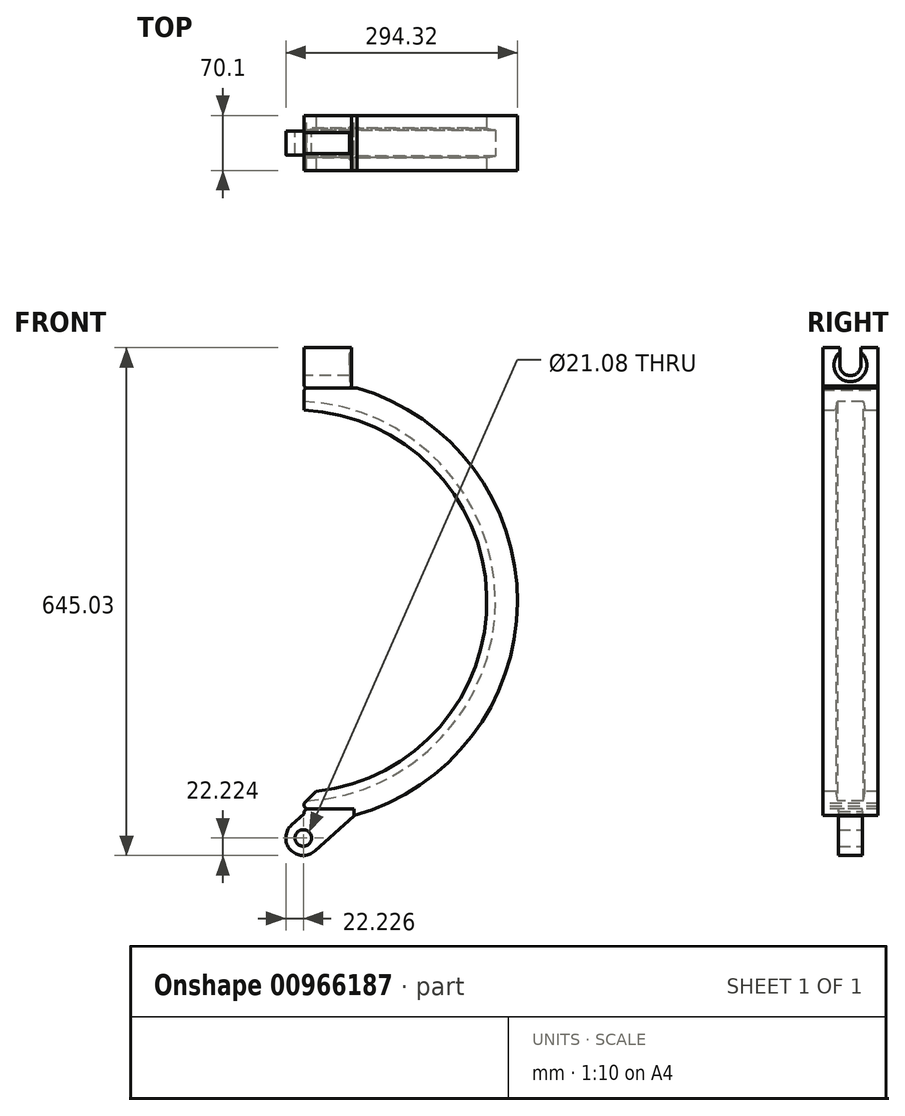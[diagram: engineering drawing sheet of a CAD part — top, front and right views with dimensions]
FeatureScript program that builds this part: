
annotation { "Feature Type Name" : "Feature", "Feature Type Description" : "" }
export const myFeature = defineFeature(function(context is Context, id is Id, definition is map)
    precondition{}
    {
        {
            var Q0;
            Q0=qCreatedBy(makeId("Front.planeOp"),FACE);
            var sketch = newSketch(context, id + "F0", { "sketchPlane" : qUnion([Q0])});
            skArc(sketch, "E0", {"start": v(11.02, -281.79) * mm, "mid": v(282, 0) * mm, "end": v(11.02, 281.79) * mm});
            skArc(sketch, "E1", {"start": v(11.02, -242.75) * mm, "mid": v(243, 0) * mm, "end": v(11.02, 242.75) * mm});
            skLineSegment(sketch, "E2", {"start": v(11.02, 281.79) * mm, "end": v(11.02, 242.75) * mm});
            skLineSegment(sketch, "E3.trimOffspring", {"start": v(11.02, -242.75) * mm, "end": v(11.02, -281.79) * mm});
            skSolve(sketch);
        }
        {
            var Q0;
            Q0=makeQuery(id+"F0.imprint","IMPRINT",FACE,{"disambiguationData":[TD([[makeQuery(id+"F0.imprint","IMPRINT",EDGE,{"derivedFrom":sQuery(id+"F0.wireOp",EDGE,"E0")}),1.0]])]});
            extrude(context, id + "F1", {"entities" : qUnion([Q0]), "depth" : 70.1 * mm, "offsetDistance" : 25.4 * mm});
        }
        {
            var Q0;
            Q0=makeQuery(id+"F1.opExtrude","SWEPT_FACE",FACE,{"disambiguationData":[OSD([sQuery(id+"F0.wireOp",EDGE,"E2")])]});
            var sketch = newSketch(context, id + "F2", { "sketchPlane" : qUnion([Q0])});
            skLineSegment(sketch, "E4", {"start": v(16.4, 242.75) * mm, "end": v(18.52, 253.68) * mm});
            skLineSegment(sketch, "E5", {"start": v(18.52, 253.68) * mm, "end": v(51.58, 253.68) * mm});
            skLineSegment(sketch, "E6", {"start": v(51.58, 253.68) * mm, "end": v(53.7, 242.75) * mm});
            skSolve(sketch);
        }
        {
            var Q0;
            {var subQ0=sQuery(id+"F2.wireOp",EDGE,"E4");Q0=makeQuery(id+"F2.imprint","IMPRINT",FACE,{"disambiguationData":[TD([[makeQuery(id+"F2.imprint","IMPRINT",EDGE,{"derivedFrom":subQ0}),-1.0]])]});}
            var Q1;
            Q1=makeQuery(id+"F1.opExtrude","CAP_EDGE",EDGE,{"disambiguationData":[OSD([sQuery(id+"F0.wireOp",EDGE,"E1")])],"isStart":false});
            revolve(context, id + "F3", {"operationType" : NewBodyOperationType.REMOVE, "surfaceOperationType" : NewSurfaceOperationType.NEW, "entities" : qUnion([Q0]), "axis" : qUnion([Q1]), "revolveType" : RevolveType.FULL, "oppositeDirection" : true});
        }
        {
            var Q0;
            Q0=makeQuery(id+"F1.opExtrude","CAP_FACE",FACE,{"disambiguationData":[OSD([sQuery(id+"F0.wireOp",EDGE,"E0"),sQuery(id+"F0.wireOp",EDGE,"E1"),sQuery(id+"F0.wireOp",EDGE,"E2"),sQuery(id+"F0.wireOp",EDGE,"E3.trimOffspring")])],"isStart":false});
            var sketch = newSketch(context, id + "F4", { "sketchPlane" : qUnion([Q0])});
            skLineSegment(sketch, "E7.bottom", {"start": v(-35.17, 306.98) * mm, "end": v(129.93, 306.98) * mm});
            skLineSegment(sketch, "E7.top", {"start": v(-35.17, 271.02) * mm, "end": v(129.93, 271.02) * mm});
            skLineSegment(sketch, "E7.left", {"start": v(-35.17, 306.98) * mm, "end": v(-35.17, 271.02) * mm});
            skLineSegment(sketch, "E7.right", {"start": v(129.93, 306.98) * mm, "end": v(129.93, 271.02) * mm});
            skLineSegment(sketch, "E8.bottom", {"start": v(-25.4, -263.65) * mm, "end": v(74.52, -263.65) * mm});
            skLineSegment(sketch, "E8.top", {"start": v(-25.4, -309.81) * mm, "end": v(74.52, -309.81) * mm});
            skLineSegment(sketch, "E8.left", {"start": v(-25.4, -263.65) * mm, "end": v(-25.4, -309.81) * mm});
            skLineSegment(sketch, "E8.right", {"start": v(74.52, -263.65) * mm, "end": v(74.52, -309.81) * mm});
            skSolve(sketch);
        }
        {
            var Q0;
            Q0 = qSketchRegion(id + "F4", true);
            extrude(context, id + "F5", {"entities" : qUnion([Q0]), "operationType" : NewBodyOperationType.REMOVE, "endBound" : BoundingType.THROUGH_ALL, "oppositeDirection" : true, "depth" : 25.4 * mm, "offsetDistance" : 25.4 * mm});
        }
        {
            var Q0;
            Q0=makeQuery(id+"F1.opExtrude","SWEPT_FACE",FACE,{"disambiguationData":[OSD([sQuery(id+"F0.wireOp",EDGE,"E2")])]});
            var sketch = newSketch(context, id + "F6", { "sketchPlane" : qUnion([Q0])});
            skLineSegment(sketch, "E9.bottom", {"start": v(0.13, 271.02) * mm, "end": v(69.98, 271.02) * mm});
            skLineSegment(sketch, "E9.top", {"start": v(0.13, 322.07) * mm, "end": v(69.98, 322.07) * mm});
            skLineSegment(sketch, "E9.left", {"start": v(0.13, 271.02) * mm, "end": v(0.13, 322.07) * mm});
            skLineSegment(sketch, "E9.right", {"start": v(69.98, 271.02) * mm, "end": v(69.98, 322.07) * mm});
            skSolve(sketch);
        }
        {
            var Q0;
            Q0 = qSketchRegion(id + "F6", true);
            extrude(context, id + "F7", {"entities" : qUnion([Q0]), "oppositeDirection" : true, "depth" : 59.94 * mm, "offsetDistance" : 25.4 * mm});
        }
        {
            var Q0;
            Q0=makeQuery(id+"F7.boolean.opBoolean","MERGE",FACE,{"derivedFrom":[makeQuery(id+"F1.opExtrude","SWEPT_FACE",FACE,{"disambiguationData":[OSD([sQuery(id+"F0.wireOp",EDGE,"E2")])]}),makeQuery(id+"F7.opExtrude","CAP_FACE",FACE,{"disambiguationData":[OSD([sQuery(id+"F6.wireOp",EDGE,"E9.bottom"),sQuery(id+"F6.wireOp",EDGE,"E9.top"),sQuery(id+"F6.wireOp",EDGE,"E9.left"),sQuery(id+"F6.wireOp",EDGE,"E9.right")])],"isStart":true})]});
            var sketch = newSketch(context, id + "F8", { "sketchPlane" : qUnion([Q0])});
            skArc(sketch, "E10", {"start": v(21.6, 299.97) * mm, "mid": v(35.05, 286.51) * mm, "end": v(48.51, 299.97) * mm});
            skPoint(sketch, "E10.centerSnap0", {"position": v(35.05, 253.68) * mm});
            skLineSegment(sketch, "E11", {"start": v(21.6, 299.97) * mm, "end": v(21.6, 322.07) * mm});
            skLineSegment(sketch, "E12", {"start": v(48.51, 299.97) * mm, "end": v(48.51, 322.07) * mm});
            skLineSegment(sketch, "E13", {"start": v(48.51, 322.07) * mm, "end": v(21.6, 322.07) * mm});
            skSolve(sketch);
        }
        {
            var Q0;
            Q0=makeQuery(id+"F8.imprint","IMPRINT",FACE,{"disambiguationData":[TD([[makeQuery(id+"F8.imprint","IMPRINT",EDGE,{"derivedFrom":sQuery(id+"F8.wireOp",EDGE,"E10")}),1.0]])]});
            extrude(context, id + "F9", {"entities" : qUnion([Q0]), "operationType" : NewBodyOperationType.REMOVE, "endBound" : BoundingType.THROUGH_ALL, "oppositeDirection" : true, "depth" : 25.4 * mm, "offsetDistance" : 25.4 * mm});
        }
        {
            var Q0;
            Q0=makeQuery(id+"F7.opExtrude","CAP_FACE",FACE,{"disambiguationData":[OSD([sQuery(id+"F6.wireOp",EDGE,"E9.bottom"),sQuery(id+"F6.wireOp",EDGE,"E9.top"),sQuery(id+"F6.wireOp",EDGE,"E9.left"),sQuery(id+"F6.wireOp",EDGE,"E9.right")])],"isStart":false});
            var sketch = newSketch(context, id + "F10", { "sketchPlane" : qUnion([Q0])});
            skCircle(sketch, "E14", {"center": v(-35.05, 299.97) * mm, "radius": 20.96 * mm});
            skSolve(sketch);
        }
        {
            var Q0;
            Q0 = qSketchRegion(id + "F10", true);
            extrude(context, id + "F11", {"entities" : qUnion([Q0]), "operationType" : NewBodyOperationType.REMOVE, "oppositeDirection" : true, "depth" : 2.54 * mm, "offsetDistance" : 25.4 * mm});
        }
        {
            var Q0;
            Q0=qCreatedBy(makeId("Front.planeOp"),FACE);
            cPlane(context, id + "F12", {"entities" : qUnion([Q0]), "cplaneType" : CPlaneType.OFFSET, "offset" : 35.05 * mm, "width" : 152.4 * mm, "height" : 152.4 * mm});
        }
        {
            var Q0;
            Q0=qCreatedBy(id+"F12.planeOp",FACE);
            var sketch = newSketch(context, id + "F13", { "sketchPlane" : qUnion([Q0])});
            skLineSegment(sketch, "E15", {"start": v(74.52, -272.46) * mm, "end": v(24.78, -317.25) * mm});
            skLineSegment(sketch, "E16", {"start": v(-4.97, -284.22) * mm, "end": v(10.82, -270) * mm});
            skCircle(sketch, "E17", {"center": v(9.9, -300.74) * mm, "radius": 10.54 * mm});
            skLineSegment(sketch, "E18", {"start": v(0, 0) * mm, "end": v(0, -72.6) * mm, "construction": true});
            skLineSegment(sketch, "E19", {"start": v(9.9, -300.74) * mm, "end": v(-19.12, -326.87) * mm, "construction": true});
            skArc(sketch, "E20", {"start": v(-4.97, -284.22) * mm, "mid": v(-6.61, -315.6) * mm, "end": v(24.78, -317.25) * mm});
            skLineSegment(sketch, "E21", {"start": v(10.82, -263.65) * mm, "end": v(10.82, -270) * mm});
            skLineSegment(sketch, "E22", {"start": v(10.82, -263.65) * mm, "end": v(74.52, -263.65) * mm});
            skLineSegment(sketch, "E23", {"start": v(74.52, -263.65) * mm, "end": v(74.52, -272.46) * mm});
            skSolve(sketch);
        }
        {
            var Q0;
            Q0 = qSketchRegion(id + "F13", true);
            extrude(context, id + "F14", {"entities" : qUnion([Q0]), "endBound" : BoundingType.SYMMETRIC, "depth" : 30.48 * mm, "offsetDistance" : 25.4 * mm});
        }
        {
            var Q0;
            Q0=makeQuery(id+"F1.opExtrude","CAP_FACE",FACE,{"disambiguationData":[OSD([sQuery(id+"F0.wireOp",EDGE,"E0"),sQuery(id+"F0.wireOp",EDGE,"E1"),sQuery(id+"F0.wireOp",EDGE,"E2"),sQuery(id+"F0.wireOp",EDGE,"E3.trimOffspring")])],"isStart":false});
            var sketch = newSketch(context, id + "F15", { "sketchPlane" : qUnion([Q0])});
            skLineSegment(sketch, "E24", {"start": v(11.02, -256.6) * mm, "end": v(26, -241.6) * mm});
            skLineSegment(sketch, "E25", {"start": v(11.02, -256.6) * mm, "end": v(11.02, -242.75) * mm});
            skArc(sketch, "E26", {"start": v(11.02, -242.75) * mm, "mid": v(18.53, -242.3) * mm, "end": v(26, -241.6) * mm});
            skSolve(sketch);
        }
        {
            var Q0;
            Q0 = qSketchRegion(id + "F15", true);
            extrude(context, id + "F16", {"entities" : qUnion([Q0]), "operationType" : NewBodyOperationType.REMOVE, "endBound" : BoundingType.THROUGH_ALL, "oppositeDirection" : true, "depth" : 25.4 * mm, "offsetDistance" : 25.4 * mm});
        }
        {
            var Q0;
            Q0=makeQuery(id+"F7.opExtrude","CAP_EDGE",EDGE,{"disambiguationData":[OSD([sQuery(id+"F6.wireOp",EDGE,"E9.bottom")])],"isStart":false});
            var Q1;
            Q1=makeQuery(id+"F7.opExtrude","CAP_EDGE",EDGE,{"disambiguationData":[OSD([sQuery(id+"F6.wireOp",EDGE,"E9.bottom")])],"isStart":true});
            chamfer(context, id + "F17", {"entities" : qUnion([Q0, Q1]), "width" : 2.54 * mm, "tangentPropagation" : true});
        }
        {
            var Q0;
            Q0=makeQuery(id+"F14.opExtrude","SWEPT_EDGE",EDGE,{"disambiguationData":[OSD([sQuery(id+"F13.wireOp",EDGE,"E22"),sQuery(id+"F13.wireOp",EDGE,"E23")])]});
            fillet(context, id + "F18", {"entities" : qUnion([Q0]), "radius" : 3.17 * mm, "tangentPropagation" : true, "allowEdgeOverflow" : false});
        }
        {
            var Q0;
            Q0=makeQuery(id+"F14.opExtrude","SWEPT_EDGE",EDGE,{"disambiguationData":[OSD([sQuery(id+"F13.wireOp",EDGE,"E21"),sQuery(id+"F13.wireOp",EDGE,"E22")])]});
            chamfer(context, id + "F19", {"entities" : qUnion([Q0]), "width" : 3.17 * mm, "tangentPropagation" : true});
        }
        {
            var Q0;
            Q0=makeQuery(id+"F5.boolean.opBoolean","INTERSECT",EDGE,{"derivedFrom":[makeQuery(id+"F1.opExtrude","SWEPT_FACE",FACE,{"disambiguationData":[OSD([sQuery(id+"F0.wireOp",EDGE,"E3.trimOffspring")])]}),makeQuery(id+"F5.opExtrude","SWEPT_FACE",FACE,{"disambiguationData":[OSD([sQuery(id+"F4.wireOp",EDGE,"E8.bottom")])]})]});
            chamfer(context, id + "F20", {"entities" : qUnion([Q0]), "width" : 3.17 * mm, "tangentPropagation" : true});
        }
        {
            var Q0;
            Q0=makeQuery(id+"F5.boolean.opBoolean","INTERSECT",EDGE,{"derivedFrom":[makeQuery(id+"F1.opExtrude","SWEPT_FACE",FACE,{"disambiguationData":[OSD([sQuery(id+"F0.wireOp",EDGE,"E2")])]}),makeQuery(id+"F5.opExtrude","SWEPT_FACE",FACE,{"disambiguationData":[OSD([sQuery(id+"F4.wireOp",EDGE,"E7.top")])]})]});
            chamfer(context, id + "F21", {"entities" : qUnion([Q0]), "width" : 2.54 * mm, "tangentPropagation" : true});
        }
    });
